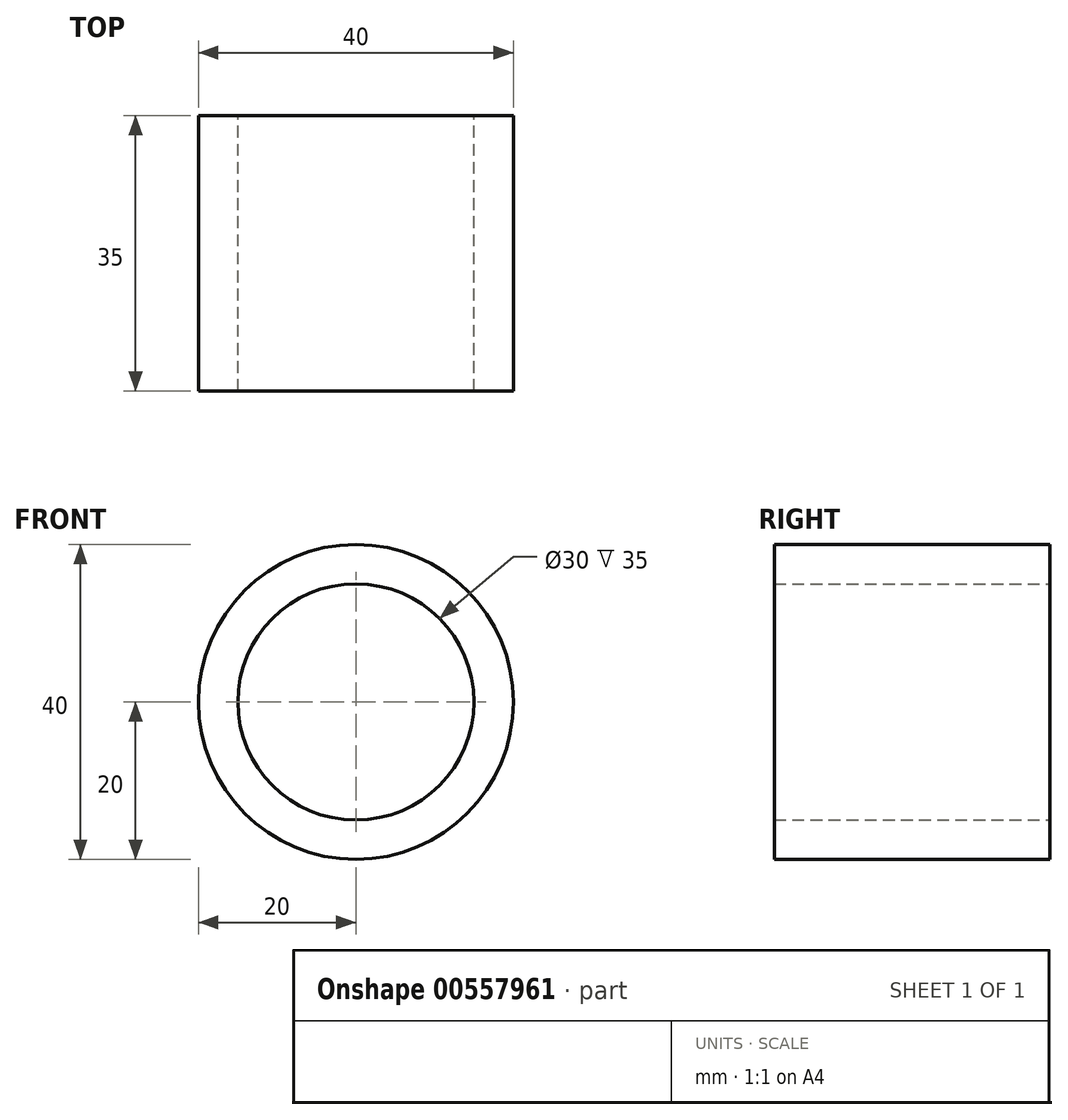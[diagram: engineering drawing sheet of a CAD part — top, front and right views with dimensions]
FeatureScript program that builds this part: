
annotation { "Feature Type Name" : "Feature", "Feature Type Description" : "" }
export const myFeature = defineFeature(function(context is Context, id is Id, definition is map)
    precondition{}
    {
        {
            var Q0;
            Q0=qCreatedBy(makeId("Front.planeOp"),FACE);
            var sketch = newSketch(context, id + "F0", { "sketchPlane" : qUnion([Q0])});
            skCircle(sketch, "E0", {"center": v(0, 0) * mm, "radius": 20 * mm});
            skCircle(sketch, "E1", {"center": v(0, 0) * mm, "radius": 15 * mm});
            skSolve(sketch);
        }
        {
            var Q0;
            Q0=makeQuery(id+"F0.imprint","IMPRINT",FACE,{"disambiguationData":[TD([[makeQuery(id+"F0.imprint","IMPRINT",EDGE,{"derivedFrom":sQuery(id+"F0.wireOp",EDGE,"E0")}),1.0]])]});
            extrude(context, id + "F1", {"entities" : qUnion([Q0]), "depth" : 35 * mm, "offsetDistance" : 25.4 * mm});
        }
    });
